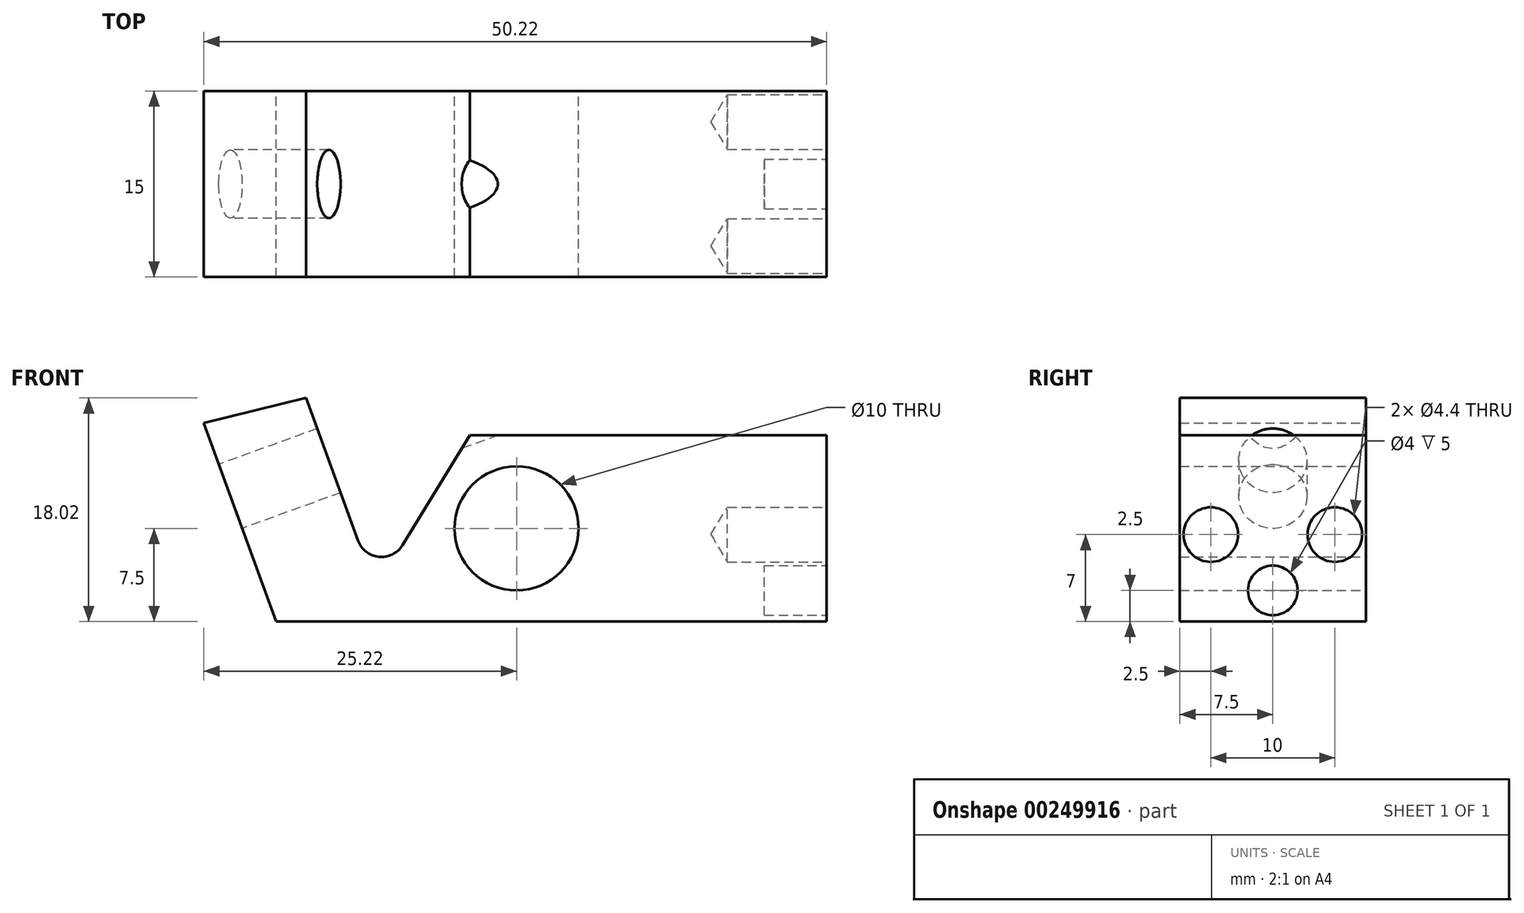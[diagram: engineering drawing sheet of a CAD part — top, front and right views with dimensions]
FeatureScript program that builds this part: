
annotation { "Feature Type Name" : "Feature", "Feature Type Description" : "" }
export const myFeature = defineFeature(function(context is Context, id is Id, definition is map)
    precondition{}
    {
        {
            var Q0;
            Q0=qCreatedBy(makeId("Front.planeOp"),FACE);
            var sketch = newSketch(context, id + "F0", { "sketchPlane" : qUnion([Q0])});
            skLineSegment(sketch, "E0", {"start": v(-8.5, 0) * mm, "end": v(35.9, 0) * mm});
            skLineSegment(sketch, "E1", {"start": v(35.9, 0) * mm, "end": v(35.9, 15) * mm});
            skLineSegment(sketch, "E2", {"start": v(35.9, 15) * mm, "end": v(7.13, 15) * mm});
            skCircle(sketch, "E3", {"center": v(10.9, 7.5) * mm, "radius": 5 * mm});
            skArc(sketch, "E4", {"start": v(-1.88, 6.52) * mm, "mid": v(-0.2, 5.21) * mm, "end": v(1.7, 6.16) * mm});
            skLineSegment(sketch, "E5", {"start": v(1.7, 6.16) * mm, "end": v(7.13, 15) * mm});
            skLineSegment(sketch, "E6", {"start": v(-8.5, 0) * mm, "end": v(-14.32, 16) * mm});
            skLineSegment(sketch, "E7", {"start": v(-14.32, 16) * mm, "end": v(-14.32, -11.43) * mm, "construction": true});
            skLineSegment(sketch, "E8", {"start": v(-1.88, 6.52) * mm, "end": v(-6.07, 18.02) * mm});
            skLineSegment(sketch, "E9", {"start": v(-14.32, 16) * mm, "end": v(-6.07, 18.02) * mm});
            skSolve(sketch);
        }
        {
            var Q0;
            Q0=makeQuery(id+"F0.imprint","IMPRINT",FACE,{"disambiguationData":[TD([[makeQuery(id+"F0.imprint","IMPRINT",EDGE,{"derivedFrom":sQuery(id+"F0.wireOp",EDGE,"E0")}),1.0]])]});
            extrude(context, id + "F1", {"entities" : qUnion([Q0]), "endBound" : BoundingType.SYMMETRIC, "depth" : 15 * mm});
        }
        {
            var Q0;
            Q0=makeQuery(id+"F1.opExtrude","SWEPT_FACE",FACE,{"disambiguationData":[OSD([sQuery(id+"F0.wireOp",EDGE,"E6")])]});
            var sketch = newSketch(context, id + "F2", { "sketchPlane" : qUnion([Q0])});
            skPoint(sketch, "E10", {"position": v(0, 13.63) * mm});
            skSolve(sketch);
        }
        {
            var Q0;
            Q0=sQuery(id+"F2.wireOp",VERTEX,"E10");
            var Q1;
            Q1=makeQuery(id+"F1.opExtrude","SWEPT_BODY",BODY,{"disambiguationData":[OSD([sQuery(id+"F0.wireOp",EDGE,"E0"),sQuery(id+"F0.wireOp",EDGE,"E1"),sQuery(id+"F0.wireOp",EDGE,"E2"),sQuery(id+"F0.wireOp",EDGE,"E3"),sQuery(id+"F0.wireOp",EDGE,"E4"),sQuery(id+"F0.wireOp",EDGE,"E5"),sQuery(id+"F0.wireOp",EDGE,"E6"),sQuery(id+"F0.wireOp",EDGE,"E8"),sQuery(id+"F0.wireOp",EDGE,"E9")])]});
            hole(context, id + "F3", {"style" : HoleStyle.SIMPLE, "endStyle" : HoleEndStyle.THROUGH, "standardTappedOrClearance" : lookupTablePath({ "standard" : "ISO", "fit" : "Normal", "size" : "M5", "type" : "Clearance" }), "standardBlindInLast" : lookupTablePath({ "fit" : "Standard", "standard" : "ISO", "size" : "M5", "type" : "Clearance" }), "holeDiameter" : 5.5 * mm, "tappedDepth" : 12 * mm, "tapClearance" : 3, "locations" : qUnion([Q0]), "scope" : qUnion([Q1])});
        }
        {
            var Q0;
            Q0=makeQuery(id+"F1.opExtrude","SWEPT_FACE",FACE,{"disambiguationData":[OSD([sQuery(id+"F0.wireOp",EDGE,"E1")])]});
            var sketch = newSketch(context, id + "F4", { "sketchPlane" : qUnion([Q0])});
            skCircle(sketch, "E11", {"center": v(0, 2.5) * mm, "radius": 2 * mm});
            skCircle(sketch, "E12", {"center": v(-5, 7) * mm, "radius": 1.5 * mm});
            skCircle(sketch, "E13", {"center": v(5, 7) * mm, "radius": 1.5 * mm});
            skSolve(sketch);
        }
        {
            var Q0;
            Q0=makeQuery(id+"F4.imprint","IMPRINT",FACE,{"disambiguationData":[TD([[makeQuery(id+"F4.imprint","IMPRINT",EDGE,{"derivedFrom":sQuery(id+"F4.wireOp",EDGE,"E11")}),1.0]])]});
            extrude(context, id + "F5", {"entities" : qUnion([Q0]), "operationType" : NewBodyOperationType.REMOVE, "oppositeDirection" : true, "depth" : 5 * mm});
        }
        {
            var Q0;
            Q0=sQuery(id+"F4.wireOp",VERTEX,"E12.center");
            var Q1;
            Q1=sQuery(id+"F4.wireOp",VERTEX,"E13.center");
            var Q2;
            Q2=makeQuery(id+"F1.opExtrude","SWEPT_BODY",BODY,{"disambiguationData":[OSD([sQuery(id+"F0.wireOp",EDGE,"E0"),sQuery(id+"F0.wireOp",EDGE,"E1"),sQuery(id+"F0.wireOp",EDGE,"E2"),sQuery(id+"F0.wireOp",EDGE,"E3"),sQuery(id+"F0.wireOp",EDGE,"E4"),sQuery(id+"F0.wireOp",EDGE,"E5"),sQuery(id+"F0.wireOp",EDGE,"E6"),sQuery(id+"F0.wireOp",EDGE,"E8"),sQuery(id+"F0.wireOp",EDGE,"E9")])]});
            hole(context, id + "F6", {"style" : HoleStyle.SIMPLE, "endStyle" : HoleEndStyle.BLIND, "standardTappedOrClearance" : lookupTablePath({ "standard" : "ISO", "fit" : "Normal", "size" : "M4", "type" : "Clearance" }), "standardBlindInLast" : lookupTablePath({ "fit" : "Standard", "standard" : "ISO", "size" : "M4", "type" : "Clearance" }), "holeDiameter" : 4.4 * mm, "holeDepth" : 8 * mm, "tappedDepth" : 12 * mm, "tapClearance" : 3, "locations" : qUnion([Q0, Q1]), "scope" : qUnion([Q2])});
        }
    });
